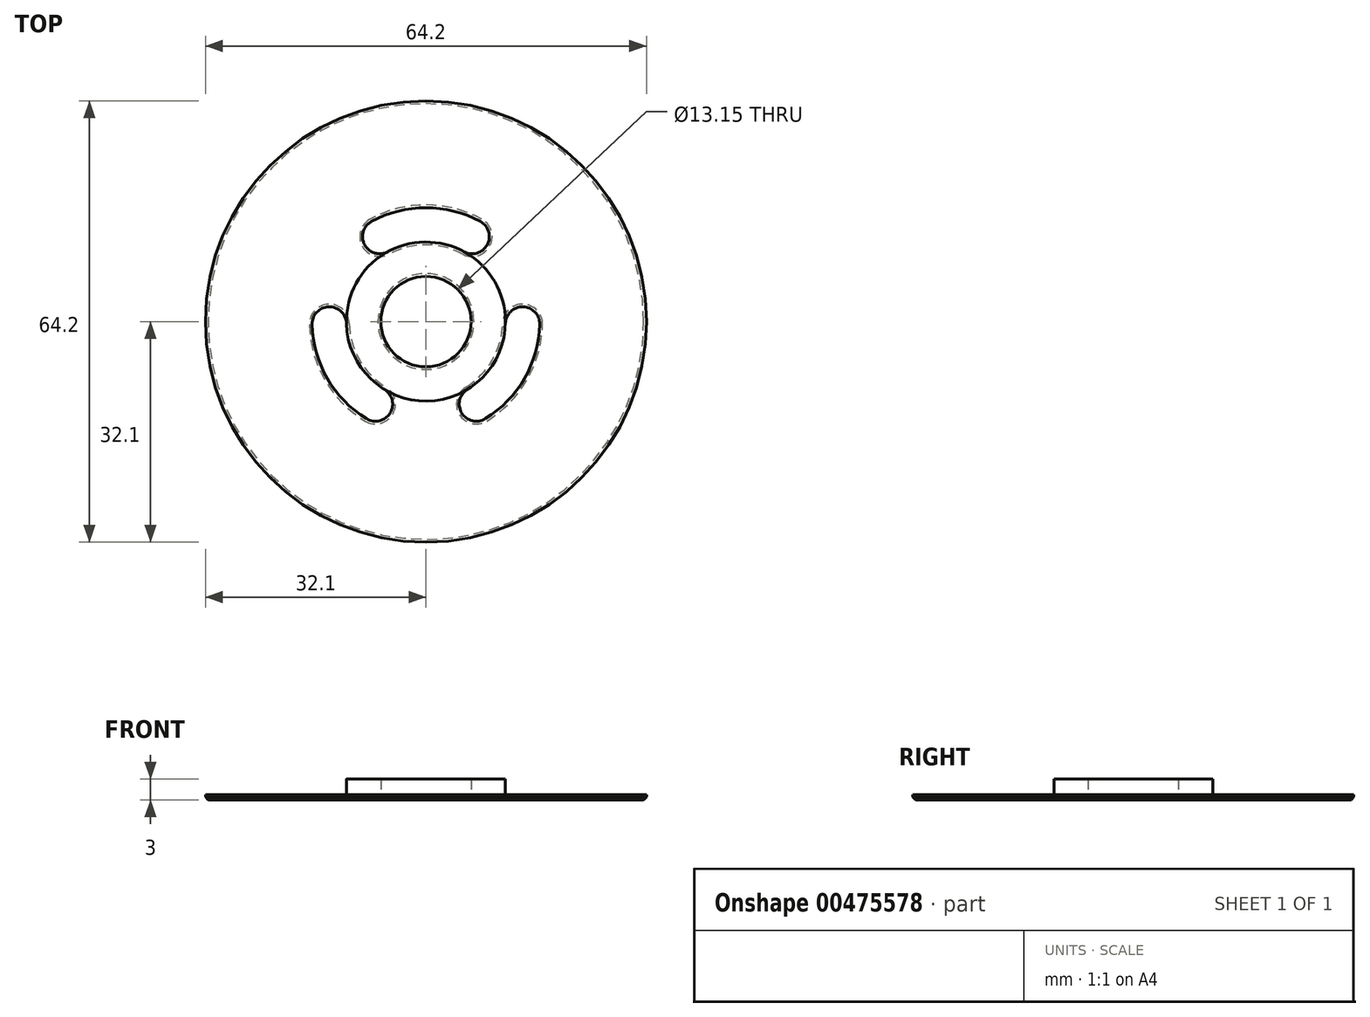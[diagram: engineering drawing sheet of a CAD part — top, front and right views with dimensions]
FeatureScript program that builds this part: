
annotation { "Feature Type Name" : "Feature", "Feature Type Description" : "" }
export const myFeature = defineFeature(function(context is Context, id is Id, definition is map)
    precondition{}
    {
        {
            var Q0;
            Q0=qCreatedBy(makeId("Top.planeOp"),FACE);
            var sketch = newSketch(context, id + "F0", { "sketchPlane" : qUnion([Q0])});
            skCircle(sketch, "E0", {"center": v(0, 0) * mm, "radius": 6.58 * mm});
            skCircle(sketch, "E1", {"center": v(0, 0) * mm, "radius": 32.1 * mm});
            skLineSegment(sketch, "E2", {"start": v(5.7, 3.29) * mm, "end": v(27.8, 16.05) * mm, "construction": true});
            skLineSegment(sketch, "E3.1.0", {"start": v(0, -6.58) * mm, "end": v(0, -32.1) * mm, "construction": true});
            skLineSegment(sketch, "E3.2.0", {"start": v(-5.7, 3.29) * mm, "end": v(-27.8, 16.05) * mm, "construction": true});
            skLineSegment(sketch, "E3.anchor1", {"start": v(0, 0) * mm, "end": v(5.7, 3.29) * mm, "construction": true});
            skLineSegment(sketch, "E3.anchor2", {"start": v(0, 0) * mm, "end": v(-5.7, 3.29) * mm, "construction": true});
            skSolve(sketch);
        }
        {
            var Q0;
            Q0=qCreatedBy(makeId("Top.planeOp"),FACE);
            var sketch = newSketch(context, id + "F1", { "sketchPlane" : qUnion([Q0])});
            skCircle(sketch, "E4.0", {"center": v(0, 0) * mm, "radius": 6.58 * mm});
            skCircle(sketch, "E5.0", {"center": v(0, 0) * mm, "radius": 11.58 * mm});
            skSolve(sketch);
        }
        {
            var Q0;
            Q0=qCreatedBy(makeId("Top.planeOp"),FACE);
            var sketch = newSketch(context, id + "F2", { "sketchPlane" : qUnion([Q0])});
            skCircle(sketch, "E6.0", {"center": v(0, 0) * mm, "radius": 11.58 * mm});
            skCircle(sketch, "E7.0", {"center": v(0, 0) * mm, "radius": 16.57 * mm, "construction": true});
            skLineSegment(sketch, "E8", {"start": v(-8.67, 10.8) * mm, "end": v(-8.67, 10.8) * mm});
            skLineSegment(sketch, "E9.MirrorCS", {"start": v(-13.69, 2.11) * mm, "end": v(-13.69, 2.11) * mm});
            skLineSegment(sketch, "E10.1.0", {"start": v(5.01, -12.91) * mm, "end": v(5.01, -12.91) * mm});
            skLineSegment(sketch, "E10.1.1", {"start": v(-5.01, -12.91) * mm, "end": v(-5.01, -12.91) * mm});
            skLineSegment(sketch, "E10.2.0", {"start": v(8.67, 10.8) * mm, "end": v(8.67, 10.8) * mm});
            skLineSegment(sketch, "E10.2.1", {"start": v(13.69, 2.11) * mm, "end": v(13.69, 2.11) * mm});
            skArc(sketch, "E11", {"start": v(-7.92, 14.56) * mm, "mid": v(0, 16.57) * mm, "end": v(7.92, 14.56) * mm});
            skArc(sketch, "E12", {"start": v(-5.53, 10.17) * mm, "mid": v(0, 11.58) * mm, "end": v(5.53, 10.17) * mm});
            skArc(sketch, "E13", {"start": v(16.57, -0.42) * mm, "mid": v(14.35, -8.29) * mm, "end": v(8.65, -14.14) * mm});
            skArc(sketch, "E14", {"start": v(11.57, -0.3) * mm, "mid": v(10.02, -5.79) * mm, "end": v(6.04, -9.87) * mm});
            skArc(sketch, "E15", {"start": v(-8.65, -14.14) * mm, "mid": v(-14.35, -8.29) * mm, "end": v(-16.57, -0.42) * mm});
            skArc(sketch, "E16", {"start": v(-6.04, -9.87) * mm, "mid": v(-10.02, -5.79) * mm, "end": v(-11.57, -0.3) * mm});
            skPoint(sketch, "E17.visualSharp", {"position": v(-7.25, 9.02) * mm});
            skArc(sketch, "E17.filletArc", {"start": v(-8.67, 10.8) * mm, "mid": v(-7.22, 9.91) * mm, "end": v(-5.53, 10.17) * mm});
            skPoint(sketch, "E18.visualSharp", {"position": v(-10.38, 12.92) * mm});
            skArc(sketch, "E18.filletArc", {"start": v(-7.92, 14.56) * mm, "mid": v(-9.18, 12.86) * mm, "end": v(-8.67, 10.8) * mm});
            skPoint(sketch, "E19.visualSharp", {"position": v(7.25, 9.02) * mm});
            skArc(sketch, "E19.filletArc", {"start": v(5.53, 10.17) * mm, "mid": v(7.22, 9.91) * mm, "end": v(8.67, 10.8) * mm});
            skPoint(sketch, "E20.visualSharp", {"position": v(10.38, 12.92) * mm});
            skArc(sketch, "E20.filletArc", {"start": v(8.67, 10.8) * mm, "mid": v(9.18, 12.86) * mm, "end": v(7.92, 14.56) * mm});
            skPoint(sketch, "E21.visualSharp", {"position": v(16.38, 2.53) * mm});
            skArc(sketch, "E21.filletArc", {"start": v(16.57, -0.42) * mm, "mid": v(15.72, 1.52) * mm, "end": v(13.69, 2.11) * mm});
            skPoint(sketch, "E22.visualSharp", {"position": v(11.44, 1.77) * mm});
            skArc(sketch, "E22.filletArc", {"start": v(13.69, 2.11) * mm, "mid": v(12.2, 1.3) * mm, "end": v(11.57, -0.3) * mm});
            skPoint(sketch, "E23.visualSharp", {"position": v(6, -15.45) * mm});
            skArc(sketch, "E23.filletArc", {"start": v(5.01, -12.91) * mm, "mid": v(6.54, -14.38) * mm, "end": v(8.65, -14.14) * mm});
            skPoint(sketch, "E24.visualSharp", {"position": v(4.2, -10.8) * mm});
            skArc(sketch, "E24.filletArc", {"start": v(6.04, -9.87) * mm, "mid": v(4.98, -11.2) * mm, "end": v(5.01, -12.91) * mm});
            skPoint(sketch, "E25.visualSharp", {"position": v(-4.2, -10.8) * mm});
            skArc(sketch, "E25.filletArc", {"start": v(-5.01, -12.91) * mm, "mid": v(-4.98, -11.2) * mm, "end": v(-6.04, -9.87) * mm});
            skPoint(sketch, "E26.visualSharp", {"position": v(-6, -15.45) * mm});
            skArc(sketch, "E26.filletArc", {"start": v(-8.65, -14.14) * mm, "mid": v(-6.54, -14.38) * mm, "end": v(-5.01, -12.91) * mm});
            skPoint(sketch, "E27.visualSharp", {"position": v(-16.38, 2.53) * mm});
            skArc(sketch, "E27.filletArc", {"start": v(-13.69, 2.11) * mm, "mid": v(-15.72, 1.52) * mm, "end": v(-16.57, -0.42) * mm});
            skPoint(sketch, "E28.visualSharp", {"position": v(-11.44, 1.77) * mm});
            skArc(sketch, "E28.filletArc", {"start": v(-11.57, -0.3) * mm, "mid": v(-12.2, 1.3) * mm, "end": v(-13.69, 2.11) * mm});
            skSolve(sketch);
        }
        {
            var Q0;
            Q0 = qSketchRegion(id + "F0", true);
            extrude(context, id + "F3", {"entities" : qUnion([Q0]), "depth" : 0.75 * mm});
        }
        {
            var Q0;
            Q0 = qSketchRegion(id + "F2", true);
            extrude(context, id + "F4", {"entities" : qUnion([Q0]), "operationType" : NewBodyOperationType.REMOVE, "depth" : 25 * mm});
        }
        {
            var Q0;
            Q0 = qSketchRegion(id + "F1", true);
            extrude(context, id + "F5", {"entities" : qUnion([Q0]), "operationType" : NewBodyOperationType.ADD, "depth" : 3 * mm});
        }
        {
            var Q0;
            Q0=makeQuery(id+"F5.boolean.opBoolean","MERGE",FACE,{"derivedFrom":[makeQuery(id+"F3.opExtrude","CAP_FACE",FACE,{"disambiguationData":[OSD([sQuery(id+"F0.wireOp",EDGE,"E0"),sQuery(id+"F0.wireOp",EDGE,"E1")])],"isStart":true}),makeQuery(id+"F5.opExtrude","CAP_FACE",FACE,{"disambiguationData":[OSD([sQuery(id+"F1.wireOp",EDGE,"E4.0"),sQuery(id+"F1.wireOp",EDGE,"E5.0")])],"isStart":true})]});
            chamfer(context, id + "F6", {"entities" : qUnion([Q0]), "width" : .4 * mm, "tangentPropagation" : true});
        }
    });
